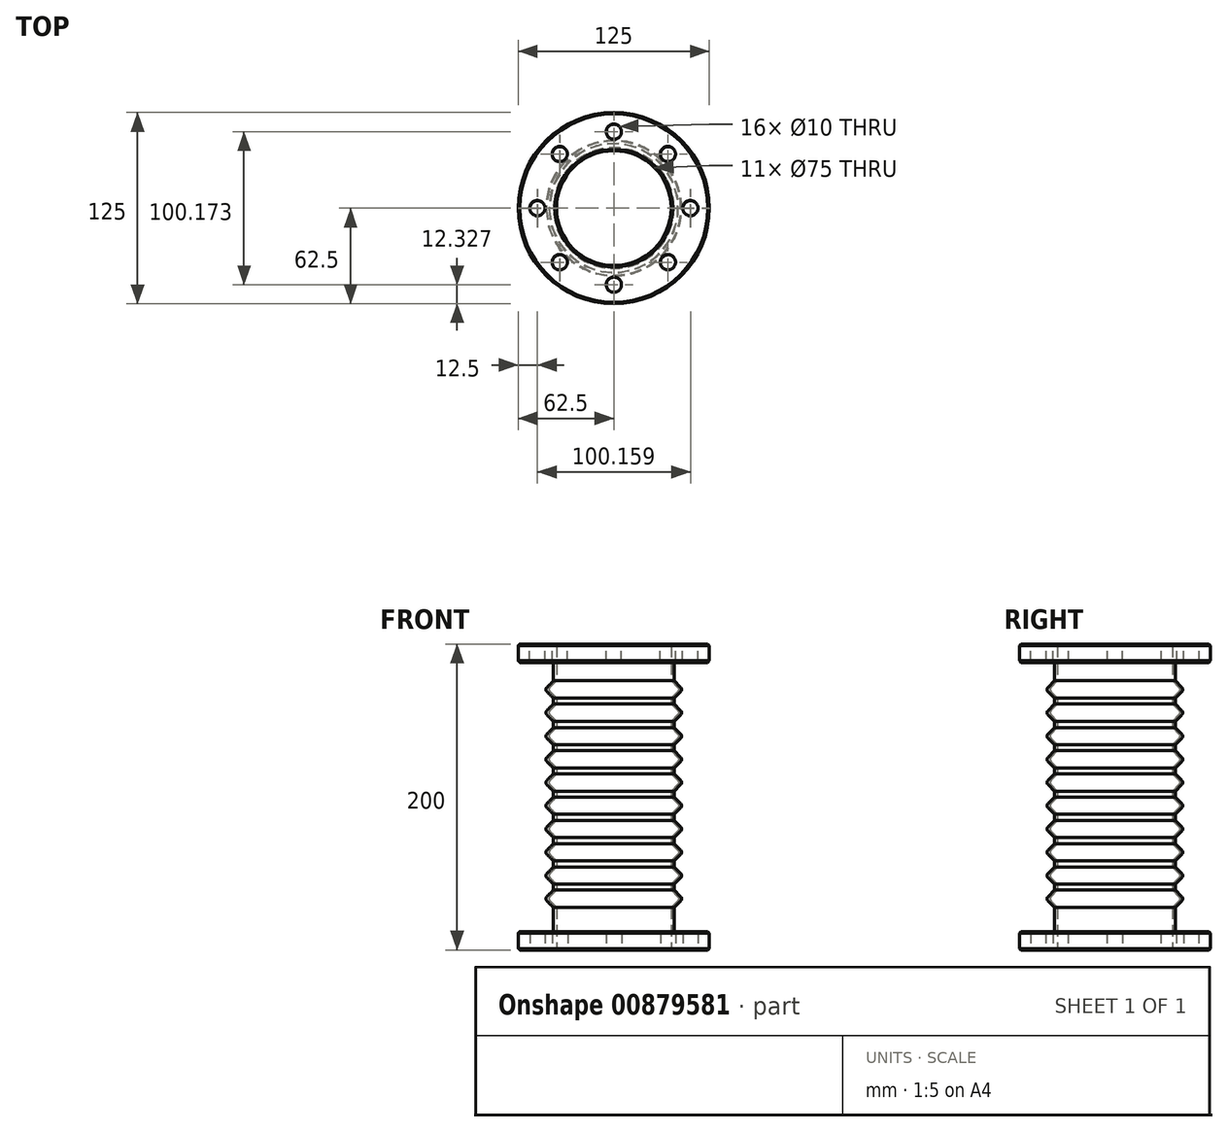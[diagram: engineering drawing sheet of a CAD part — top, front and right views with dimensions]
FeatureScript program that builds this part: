
annotation { "Feature Type Name" : "Feature", "Feature Type Description" : "" }
export const myFeature = defineFeature(function(context is Context, id is Id, definition is map)
    precondition{}
    {
        {
            var Q0;
            Q0=qCreatedBy(makeId("Front.planeOp"),FACE);
            var sketch = newSketch(context, id + "F0", { "sketchPlane" : qUnion([Q0])});
            skLineSegment(sketch, "E0", {"start": v(0, 0) * mm, "end": v(0, 200) * mm, "construction": true});
            skLineSegment(sketch, "E1.bottom", {"start": v(37.5, 0) * mm, "end": v(62.5, 0) * mm});
            skLineSegment(sketch, "E1.top", {"start": v(37.5, 12) * mm, "end": v(62.5, 12) * mm});
            skLineSegment(sketch, "E1.left", {"start": v(37.5, 0) * mm, "end": v(37.5, 12) * mm});
            skLineSegment(sketch, "E1.right", {"start": v(62.5, 0) * mm, "end": v(62.5, 12) * mm});
            skLineSegment(sketch, "E2.bottom", {"start": v(37.5, 188) * mm, "end": v(62.5, 188) * mm});
            skLineSegment(sketch, "E2.top", {"start": v(37.5, 200) * mm, "end": v(62.5, 200) * mm});
            skLineSegment(sketch, "E2.left", {"start": v(37.5, 188) * mm, "end": v(37.5, 200) * mm});
            skLineSegment(sketch, "E2.right", {"start": v(62.5, 188) * mm, "end": v(62.5, 200) * mm});
            skLineSegment(sketch, "E3", {"start": v(49.12, 188) * mm, "end": v(37.5, 188) * mm});
            skLineSegment(sketch, "E4", {"start": v(37.5, 12) * mm, "end": v(37.5, 24) * mm});
            skLineSegment(sketch, "E5", {"start": v(37.5, 176.04) * mm, "end": v(41.74, 171.8) * mm});
            skLineSegment(sketch, "E6", {"start": v(41.74, 168.97) * mm, "end": v(37.5, 164.73) * mm});
            skLineSegment(sketch, "E7", {"start": v(37.5, 160.85) * mm, "end": v(41.74, 156.61) * mm});
            skLineSegment(sketch, "E8", {"start": v(41.74, 153.78) * mm, "end": v(37.5, 149.54) * mm});
            skLineSegment(sketch, "E9", {"start": v(37.5, 145.51) * mm, "end": v(41.74, 141.27) * mm});
            skLineSegment(sketch, "E10", {"start": v(41.74, 138.44) * mm, "end": v(37.5, 134.2) * mm});
            skLineSegment(sketch, "E11", {"start": v(37.5, 130.3) * mm, "end": v(41.74, 126.06) * mm});
            skLineSegment(sketch, "E12", {"start": v(41.74, 123.24) * mm, "end": v(37.5, 119) * mm});
            skLineSegment(sketch, "E13", {"start": v(37.5, 119) * mm, "end": v(37.5, 115.1) * mm});
            skLineSegment(sketch, "E14", {"start": v(37.5, 115.14) * mm, "end": v(41.74, 110.9) * mm});
            skLineSegment(sketch, "E15", {"start": v(41.74, 108.07) * mm, "end": v(37.5, 103.82) * mm});
            skLineSegment(sketch, "E16", {"start": v(37.5, 100.01) * mm, "end": v(41.74, 95.77) * mm});
            skLineSegment(sketch, "E17", {"start": v(41.74, 92.94) * mm, "end": v(37.5, 88.7) * mm});
            skLineSegment(sketch, "E18", {"start": v(37.5, 88.7) * mm, "end": v(37.5, 84.81) * mm});
            skLineSegment(sketch, "E19", {"start": v(41.75, 77.7) * mm, "end": v(37.5, 73.45) * mm});
            skLineSegment(sketch, "E20", {"start": v(37.5, 73.45) * mm, "end": v(37.5, 69.56) * mm});
            skLineSegment(sketch, "E21", {"start": v(41.74, 62.48) * mm, "end": v(37.5, 58.24) * mm});
            skLineSegment(sketch, "E22", {"start": v(37.5, 58.24) * mm, "end": v(37.5, 54.35) * mm});
            skLineSegment(sketch, "E23", {"start": v(41.75, 47.23) * mm, "end": v(37.5, 42.98) * mm});
            skLineSegment(sketch, "E24", {"start": v(37.5, 42.98) * mm, "end": v(37.5, 39.1) * mm});
            skLineSegment(sketch, "E25", {"start": v(37.5, 39.2) * mm, "end": v(41.74, 34.96) * mm});
            skLineSegment(sketch, "E26", {"start": v(41.74, 32.13) * mm, "end": v(37.5, 27.89) * mm});
            skLineSegment(sketch, "E27", {"start": v(37.5, 27.89) * mm, "end": v(37.5, 24) * mm});
            skLineSegment(sketch, "E28", {"start": v(43.74, 168.93) * mm, "end": v(39.5, 164.69) * mm});
            skLineSegment(sketch, "E29", {"start": v(39.5, 164.69) * mm, "end": v(39.5, 160.8) * mm});
            skLineSegment(sketch, "E30", {"start": v(39.5, 160.82) * mm, "end": v(43.74, 156.57) * mm});
            skLineSegment(sketch, "E31", {"start": v(43.74, 153.74) * mm, "end": v(39.44, 149.44) * mm});
            skLineSegment(sketch, "E32", {"start": v(39.44, 149.44) * mm, "end": v(39.44, 145.44) * mm});
            skLineSegment(sketch, "E33", {"start": v(43.73, 138.4) * mm, "end": v(39.5, 134.16) * mm});
            skLineSegment(sketch, "E34", {"start": v(39.5, 134.16) * mm, "end": v(39.5, 130.27) * mm});
            skLineSegment(sketch, "E35", {"start": v(43.74, 123.2) * mm, "end": v(39.5, 118.95) * mm});
            skLineSegment(sketch, "E36", {"start": v(39.5, 118.95) * mm, "end": v(39.5, 115.07) * mm});
            skLineSegment(sketch, "E37", {"start": v(39.5, 115.14) * mm, "end": v(43.74, 110.9) * mm});
            skLineSegment(sketch, "E38", {"start": v(43.74, 108.07) * mm, "end": v(39.5, 103.82) * mm});
            skLineSegment(sketch, "E39", {"start": v(39.5, 103.82) * mm, "end": v(39.5, 99.94) * mm});
            skLineSegment(sketch, "E40", {"start": v(39.5, 100.01) * mm, "end": v(43.74, 95.77) * mm});
            skLineSegment(sketch, "E41", {"start": v(43.74, 92.94) * mm, "end": v(39.5, 88.7) * mm});
            skLineSegment(sketch, "E42", {"start": v(39.5, 88.7) * mm, "end": v(39.5, 84.81) * mm});
            skLineSegment(sketch, "E43", {"start": v(43.75, 77.7) * mm, "end": v(39.5, 73.45) * mm});
            skLineSegment(sketch, "E44", {"start": v(39.5, 73.45) * mm, "end": v(39.5, 69.56) * mm});
            skLineSegment(sketch, "E45", {"start": v(43.74, 62.48) * mm, "end": v(39.5, 58.24) * mm});
            skLineSegment(sketch, "E46", {"start": v(39.5, 58.24) * mm, "end": v(39.5, 54.35) * mm});
            skLineSegment(sketch, "E47", {"start": v(43.75, 47.23) * mm, "end": v(39.5, 42.98) * mm});
            skLineSegment(sketch, "E48", {"start": v(39.5, 42.98) * mm, "end": v(39.5, 39.1) * mm});
            skLineSegment(sketch, "E49", {"start": v(39.5, 39.2) * mm, "end": v(43.74, 34.96) * mm});
            skLineSegment(sketch, "E50", {"start": v(43.74, 32.13) * mm, "end": v(39.5, 27.89) * mm});
            skLineSegment(sketch, "E51", {"start": v(43.74, 171.76) * mm, "end": v(39.5, 176) * mm});
            skLineSegment(sketch, "E52", {"start": v(39.5, 27.89) * mm, "end": v(39.5, 24) * mm});
            skLineSegment(sketch, "E53", {"start": v(37.5, 100.01) * mm, "end": v(37.5, 103.82) * mm});
            skLineSegment(sketch, "E54", {"start": v(37.5, 130.3) * mm, "end": v(37.5, 134.2) * mm});
            skLineSegment(sketch, "E55", {"start": v(37.5, 145.51) * mm, "end": v(37.5, 149.54) * mm});
            skLineSegment(sketch, "E56", {"start": v(37.5, 160.85) * mm, "end": v(37.5, 164.73) * mm});
            skLineSegment(sketch, "E57", {"start": v(39.5, 176) * mm, "end": v(39.5, 188) * mm});
            skLineSegment(sketch, "E58", {"start": v(37.5, 176.04) * mm, "end": v(37.5, 188) * mm});
            skLineSegment(sketch, "E59", {"start": v(39.5, 24) * mm, "end": v(39.5, 12) * mm});
            skLineSegment(sketch, "E60", {"start": v(39.5, 12) * mm, "end": v(39.5, 27.89) * mm});
            skLineSegment(sketch, "E61", {"start": v(39.44, 145.44) * mm, "end": v(43.72, 141.23) * mm});
            skLineSegment(sketch, "E62", {"start": v(43.74, 126.02) * mm, "end": v(39.5, 130.27) * mm});
            skLineSegment(sketch, "E63", {"start": v(43.76, 80.52) * mm, "end": v(39.5, 84.81) * mm});
            skLineSegment(sketch, "E64", {"start": v(41.76, 80.52) * mm, "end": v(37.5, 84.81) * mm});
            skLineSegment(sketch, "E65", {"start": v(39.5, 69.56) * mm, "end": v(43.75, 65.3) * mm});
            skLineSegment(sketch, "E66", {"start": v(37.5, 69.56) * mm, "end": v(41.75, 65.3) * mm});
            skLineSegment(sketch, "E67", {"start": v(41.76, 50.05) * mm, "end": v(37.5, 54.35) * mm});
            skLineSegment(sketch, "E68", {"start": v(43.76, 50.05) * mm, "end": v(39.5, 54.35) * mm});
            skPoint(sketch, "E69.visualSharp", {"position": v(43.16, 170.38) * mm});
            skArc(sketch, "E69.filletArc", {"start": v(41.74, 168.97) * mm, "mid": v(42.33, 170.38) * mm, "end": v(41.74, 171.8) * mm});
            skPoint(sketch, "E70.visualSharp", {"position": v(45.16, 170.34) * mm});
            skArc(sketch, "E70.filletArc", {"start": v(43.74, 168.93) * mm, "mid": v(44.33, 170.34) * mm, "end": v(43.74, 171.76) * mm});
            skPoint(sketch, "E71.visualSharp", {"position": v(43.16, 155.2) * mm});
            skArc(sketch, "E71.filletArc", {"start": v(41.74, 153.78) * mm, "mid": v(42.33, 155.2) * mm, "end": v(41.74, 156.61) * mm});
            skPoint(sketch, "E72.visualSharp", {"position": v(45.16, 155.16) * mm});
            skArc(sketch, "E72.filletArc", {"start": v(43.74, 153.74) * mm, "mid": v(44.33, 155.16) * mm, "end": v(43.74, 156.57) * mm});
            skPoint(sketch, "E73.visualSharp", {"position": v(43.16, 139.86) * mm});
            skArc(sketch, "E73.filletArc", {"start": v(41.74, 138.44) * mm, "mid": v(42.33, 139.86) * mm, "end": v(41.74, 141.27) * mm});
            skPoint(sketch, "E74.visualSharp", {"position": v(45.16, 139.82) * mm});
            skArc(sketch, "E74.filletArc", {"start": v(43.73, 138.4) * mm, "mid": v(44.32, 139.81) * mm, "end": v(43.72, 141.23) * mm});
            skPoint(sketch, "E75.visualSharp", {"position": v(43.16, 124.65) * mm});
            skArc(sketch, "E75.filletArc", {"start": v(41.74, 123.24) * mm, "mid": v(42.33, 124.65) * mm, "end": v(41.74, 126.06) * mm});
            skPoint(sketch, "E76.visualSharp", {"position": v(45.16, 124.61) * mm});
            skArc(sketch, "E76.filletArc", {"start": v(43.74, 123.2) * mm, "mid": v(44.33, 124.61) * mm, "end": v(43.74, 126.02) * mm});
            skPoint(sketch, "E77.visualSharp", {"position": v(43.16, 109.48) * mm});
            skArc(sketch, "E77.filletArc", {"start": v(41.74, 108.07) * mm, "mid": v(42.33, 109.48) * mm, "end": v(41.74, 110.9) * mm});
            skPoint(sketch, "E78.visualSharp", {"position": v(45.16, 109.48) * mm});
            skArc(sketch, "E78.filletArc", {"start": v(43.74, 108.07) * mm, "mid": v(44.33, 109.48) * mm, "end": v(43.74, 110.9) * mm});
            skPoint(sketch, "E79.visualSharp", {"position": v(43.16, 94.35) * mm});
            skArc(sketch, "E79.filletArc", {"start": v(41.74, 92.94) * mm, "mid": v(42.33, 94.35) * mm, "end": v(41.74, 95.77) * mm});
            skPoint(sketch, "E80.visualSharp", {"position": v(45.16, 94.35) * mm});
            skArc(sketch, "E80.filletArc", {"start": v(43.74, 92.94) * mm, "mid": v(44.33, 94.35) * mm, "end": v(43.74, 95.77) * mm});
            skPoint(sketch, "E81.visualSharp", {"position": v(43.16, 79.1) * mm});
            skArc(sketch, "E81.filletArc", {"start": v(41.75, 77.7) * mm, "mid": v(42.33, 79.1) * mm, "end": v(41.76, 80.52) * mm});
            skPoint(sketch, "E82.visualSharp", {"position": v(45.16, 79.1) * mm});
            skArc(sketch, "E82.filletArc", {"start": v(43.75, 77.7) * mm, "mid": v(44.33, 79.1) * mm, "end": v(43.76, 80.52) * mm});
            skPoint(sketch, "E83.visualSharp", {"position": v(43.16, 63.9) * mm});
            skArc(sketch, "E83.filletArc", {"start": v(41.74, 62.48) * mm, "mid": v(42.33, 63.9) * mm, "end": v(41.75, 65.3) * mm});
            skPoint(sketch, "E84.visualSharp", {"position": v(45.16, 63.9) * mm});
            skArc(sketch, "E84.filletArc", {"start": v(43.74, 62.48) * mm, "mid": v(44.33, 63.9) * mm, "end": v(43.75, 65.3) * mm});
            skPoint(sketch, "E85.visualSharp", {"position": v(43.16, 48.64) * mm});
            skArc(sketch, "E85.filletArc", {"start": v(41.75, 47.23) * mm, "mid": v(42.34, 48.64) * mm, "end": v(41.76, 50.05) * mm});
            skPoint(sketch, "E86.visualSharp", {"position": v(45.16, 48.64) * mm});
            skArc(sketch, "E86.filletArc", {"start": v(43.75, 47.23) * mm, "mid": v(44.34, 48.64) * mm, "end": v(43.76, 50.05) * mm});
            skPoint(sketch, "E87.visualSharp", {"position": v(43.16, 33.54) * mm});
            skArc(sketch, "E87.filletArc", {"start": v(41.74, 32.13) * mm, "mid": v(42.33, 33.54) * mm, "end": v(41.74, 34.96) * mm});
            skPoint(sketch, "E88.visualSharp", {"position": v(45.16, 33.54) * mm});
            skArc(sketch, "E88.filletArc", {"start": v(43.74, 32.13) * mm, "mid": v(44.33, 33.54) * mm, "end": v(43.74, 34.96) * mm});
            skSolve(sketch);
        }
        {
            var Q0;
            {var subQ0=sQuery(id+"F0.wireOp",EDGE,"7JNMCSmd-nJx8-slAp-5Nux-Cu1BHQG4eeL3");Q0=makeQuery(id+"F0.imprint","IMPRINT",FACE,{"disambiguationData":[TD([[makeQuery(id+"F0.imprint","IMPRINT",EDGE,{"derivedFrom":subQ0}),-1.0]])]});}
            var Q1;
            Q1=makeQuery(id+"F0.imprint","IMPRINT",FACE,{"disambiguationData":[TD([[makeQuery(id+"F0.imprint","IMPRINT",EDGE,{"derivedFrom":sQuery(id+"F0.wireOp",EDGE,"E2.bottom")}),1.0]])]});
            var Q2;
            Q2=makeQuery(id+"F0.imprint","IMPRINT",FACE,{"disambiguationData":[TD([[makeQuery(id+"F0.imprint","IMPRINT",EDGE,{"derivedFrom":sQuery(id+"F0.wireOp",EDGE,"E1.bottom")}),1.0]])]});
            var Q3;
            {var subQ13=sQuery(id+"F0.wireOp",EDGE,"E4");Q3=makeQuery(id+"F0.imprint","IMPRINT",FACE,{"disambiguationData":[TD([[makeQuery(id+"F0.imprint","IMPRINT",EDGE,{"derivedFrom":subQ13}),-1.0]])]});}
            var Q4;
            Q4=sQuery(id+"F0.wireOp",EDGE,"E0");
            revolve(context, id + "F1", {"surfaceOperationType" : NewSurfaceOperationType.NEW, "entities" : qUnion([Q0, Q1, Q2, Q3]), "axis" : qUnion([Q4]), "revolveType" : RevolveType.FULL});
        }
        {
            var Q0;
            Q0=makeQuery(id+"F1.opRevolve","SWEPT_FACE",FACE,{"disambiguationData":[OSD([sQuery(id+"F0.wireOp",EDGE,"E2.top")])]});
            var sketch = newSketch(context, id + "F2", { "sketchPlane" : qUnion([Q0])});
            skCircle(sketch, "E89", {"center": v(0, 0) * mm, "radius": 50 * mm});
            skLineSegment(sketch, "E90", {"start": v(0, 0) * mm, "end": v(-50, 0) * mm});
            skLineSegment(sketch, "E91", {"start": v(0, 0) * mm, "end": v(0, 50) * mm});
            skLineSegment(sketch, "E92", {"start": v(0, 0) * mm, "end": v(-35.36, 35.36) * mm});
            skLineSegment(sketch, "E93", {"start": v(0, 0) * mm, "end": v(50, 0) * mm});
            skLineSegment(sketch, "E94", {"start": v(0, 0) * mm, "end": v(35.36, 35.36) * mm});
            skLineSegment(sketch, "E95", {"start": v(0, 0) * mm, "end": v(35.36, -35.36) * mm});
            skLineSegment(sketch, "E96", {"start": v(0, 0) * mm, "end": v(0, -50) * mm});
            skLineSegment(sketch, "E97", {"start": v(0, 0) * mm, "end": v(-35.36, -35.36) * mm});
            skSolve(sketch);
        }
        {
            var Q0;
            Q0=sQuery(id+"F2.wireOp",VERTEX,"E90.end");
            var Q1;
            Q1=sQuery(id+"F2.wireOp",VERTEX,"E92.end");
            var Q2;
            Q2=sQuery(id+"F2.wireOp",VERTEX,"E91.end");
            var Q3;
            Q3=sQuery(id+"F2.wireOp",VERTEX,"E94.end");
            var Q4;
            Q4=sQuery(id+"F2.wireOp",VERTEX,"E93.end");
            var Q5;
            Q5=sQuery(id+"F2.wireOp",VERTEX,"E95.end");
            var Q6;
            Q6=sQuery(id+"F2.wireOp",VERTEX,"E96.end");
            var Q7;
            Q7=sQuery(id+"F2.wireOp",VERTEX,"E97.end");
            var Q8;
            Q8=makeQuery(id+"F1.opRevolve","SWEPT_BODY",BODY,{"disambiguationData":[OSD([sQuery(id+"F0.wireOp",EDGE,"E1.bottom"),sQuery(id+"F0.wireOp",EDGE,"E1.top"),sQuery(id+"F0.wireOp",EDGE,"E1.left"),sQuery(id+"F0.wireOp",EDGE,"E1.right"),sQuery(id+"F0.wireOp",EDGE,"E2.bottom"),sQuery(id+"F0.wireOp",EDGE,"E2.top"),sQuery(id+"F0.wireOp",EDGE,"E2.left"),sQuery(id+"F0.wireOp",EDGE,"E2.right"),sQuery(id+"F0.wireOp",EDGE,"7JNMCSmd-nJx8-slAp-5Nux-Cu1BHQG4eeL3"),sQuery(id+"F0.wireOp",EDGE,"xSUHY1hX-u8nV-SjKD-2nK2-6XUFaaVvMroe"),sQuery(id+"F0.wireOp",EDGE,"rQDTT3AA-Bt1S-jRNE-MUDb-fmsf6ePG7gEG"),sQuery(id+"F0.wireOp",EDGE,"25a1cL4V-paF4-rwCJ-306o-4v5FNgoqHX95"),sQuery(id+"F0.wireOp",EDGE,"bOkS3g0W-cvPP-gkzR-AXlQ-F5RIaoCkBvoo"),sQuery(id+"F0.wireOp",EDGE,"DAgTOG4h-LVyY-aJrt-t6WS-GQ4c7HnX23bk"),sQuery(id+"F0.wireOp",EDGE,"wgsqm14R-cCDp-ybnt-tiYT-U1sHfBOHY4Df"),sQuery(id+"F0.wireOp",EDGE,"77dda6b8-0e61-492f-92f8-d2d185dd74d5.filletArc"),sQuery(id+"F0.wireOp",EDGE,"0257c514-efe3-423c-bb2b-4c4e0ae5e3d5.filletArc"),sQuery(id+"F0.wireOp",EDGE,"e251e59c-608a-4d9b-9d9d-7884a468bad4.filletArc"),sQuery(id+"F0.wireOp",EDGE,"1fcf53c9-d44e-426e-92d8-455222d8480c.filletArc"),sQuery(id+"F0.wireOp",EDGE,"723f02ad-6a34-478a-827c-48895c4f980a.filletArc"),sQuery(id+"F0.wireOp",EDGE,"36326b0e-995e-4fdb-9748-851bf4a9242e.filletArc"),sQuery(id+"F0.wireOp",EDGE,"f7893906-4d7b-4bea-b248-10763c51d39d.0"),sQuery(id+"F0.wireOp",EDGE,"f7893906-4d7b-4bea-b248-10763c51d39d.1"),sQuery(id+"F0.wireOp",EDGE,"f7893906-4d7b-4bea-b248-10763c51d39d.2"),sQuery(id+"F0.wireOp",EDGE,"f7893906-4d7b-4bea-b248-10763c51d39d.3"),sQuery(id+"F0.wireOp",EDGE,"f7893906-4d7b-4bea-b248-10763c51d39d.4"),sQuery(id+"F0.wireOp",EDGE,"f7893906-4d7b-4bea-b248-10763c51d39d.5"),sQuery(id+"F0.wireOp",EDGE,"f7893906-4d7b-4bea-b248-10763c51d39d.6"),sQuery(id+"F0.wireOp",EDGE,"f7893906-4d7b-4bea-b248-10763c51d39d.7"),sQuery(id+"F0.wireOp",EDGE,"f7893906-4d7b-4bea-b248-10763c51d39d.8"),sQuery(id+"F0.wireOp",EDGE,"f7893906-4d7b-4bea-b248-10763c51d39d.9"),sQuery(id+"F0.wireOp",EDGE,"f7893906-4d7b-4bea-b248-10763c51d39d.10"),sQuery(id+"F0.wireOp",EDGE,"zz77thpP-ZF6f-9Xch-fK0u-6JuafN0EIoVi"),sQuery(id+"F0.wireOp",EDGE,"MnvxiiVR-vjBi-grum-E19G-Wj8JN0Ya69Xf")])]});
            hole(context, id + "F3", {"style" : HoleStyle.SIMPLE, "endStyle" : HoleEndStyle.BLIND, "holeDiameter" : 10 * mm, "majorDiameter" : 5 * mm, "holeDepth" : 20 * mm, "isTappedThrough" : true, "tappedDepth" : 12 * mm, "tapClearance" : 3, "locations" : qUnion([Q0, Q1, Q2, Q3, Q4, Q5, Q6, Q7]), "scope" : qUnion([Q8])});
        }
        {
            var Q0;
            Q0=makeQuery(id+"F1.opRevolve","SWEPT_FACE",FACE,{"disambiguationData":[OSD([sQuery(id+"F0.wireOp",EDGE,"E1.bottom")])]});
            var sketch = newSketch(context, id + "F4", { "sketchPlane" : qUnion([Q0])});
            skCircle(sketch, "E98", {"center": v(0.16, 0.17) * mm, "radius": 50 * mm});
            skLineSegment(sketch, "E99", {"start": v(0.16, 0.17) * mm, "end": v(-49.84, 0.17) * mm});
            skLineSegment(sketch, "E100", {"start": v(0.16, 0.17) * mm, "end": v(0.16, 50.17) * mm});
            skLineSegment(sketch, "E101", {"start": v(0.16, 0.17) * mm, "end": v(-35.2, 35.53) * mm});
            skLineSegment(sketch, "E102", {"start": v(0.16, 0.17) * mm, "end": v(50.16, 0.17) * mm});
            skLineSegment(sketch, "E103", {"start": v(0.16, 0.17) * mm, "end": v(35.51, 35.53) * mm});
            skLineSegment(sketch, "E104", {"start": v(0.16, 0.17) * mm, "end": v(35.51, -35.18) * mm});
            skLineSegment(sketch, "E105", {"start": v(0.16, 0.17) * mm, "end": v(0.16, -49.83) * mm});
            skLineSegment(sketch, "E106", {"start": v(0.16, 0.17) * mm, "end": v(-35.2, -35.18) * mm});
            skSolve(sketch);
        }
        {
            var Q0;
            Q0=sQuery(id+"F4.wireOp",VERTEX,"E105.end");
            var Q1;
            Q1=sQuery(id+"F4.wireOp",VERTEX,"E106.end");
            var Q2;
            Q2=sQuery(id+"F4.wireOp",VERTEX,"E99.end");
            var Q3;
            Q3=sQuery(id+"F4.wireOp",VERTEX,"E101.end");
            var Q4;
            Q4=sQuery(id+"F4.wireOp",VERTEX,"E100.end");
            var Q5;
            Q5=sQuery(id+"F4.wireOp",VERTEX,"E103.end");
            var Q6;
            Q6=sQuery(id+"F4.wireOp",VERTEX,"E102.end");
            var Q7;
            Q7=sQuery(id+"F4.wireOp",VERTEX,"E104.end");
            var Q8;
            Q8=makeQuery(id+"F1.opRevolve","SWEPT_BODY",BODY,{"disambiguationData":[OSD([sQuery(id+"F0.wireOp",EDGE,"E1.bottom"),sQuery(id+"F0.wireOp",EDGE,"E1.top"),sQuery(id+"F0.wireOp",EDGE,"E1.left"),sQuery(id+"F0.wireOp",EDGE,"E1.right"),sQuery(id+"F0.wireOp",EDGE,"E2.bottom"),sQuery(id+"F0.wireOp",EDGE,"E2.top"),sQuery(id+"F0.wireOp",EDGE,"E2.left"),sQuery(id+"F0.wireOp",EDGE,"E2.right"),sQuery(id+"F0.wireOp",EDGE,"7JNMCSmd-nJx8-slAp-5Nux-Cu1BHQG4eeL3"),sQuery(id+"F0.wireOp",EDGE,"xSUHY1hX-u8nV-SjKD-2nK2-6XUFaaVvMroe"),sQuery(id+"F0.wireOp",EDGE,"rQDTT3AA-Bt1S-jRNE-MUDb-fmsf6ePG7gEG"),sQuery(id+"F0.wireOp",EDGE,"25a1cL4V-paF4-rwCJ-306o-4v5FNgoqHX95"),sQuery(id+"F0.wireOp",EDGE,"bOkS3g0W-cvPP-gkzR-AXlQ-F5RIaoCkBvoo"),sQuery(id+"F0.wireOp",EDGE,"DAgTOG4h-LVyY-aJrt-t6WS-GQ4c7HnX23bk"),sQuery(id+"F0.wireOp",EDGE,"wgsqm14R-cCDp-ybnt-tiYT-U1sHfBOHY4Df"),sQuery(id+"F0.wireOp",EDGE,"77dda6b8-0e61-492f-92f8-d2d185dd74d5.filletArc"),sQuery(id+"F0.wireOp",EDGE,"0257c514-efe3-423c-bb2b-4c4e0ae5e3d5.filletArc"),sQuery(id+"F0.wireOp",EDGE,"e251e59c-608a-4d9b-9d9d-7884a468bad4.filletArc"),sQuery(id+"F0.wireOp",EDGE,"1fcf53c9-d44e-426e-92d8-455222d8480c.filletArc"),sQuery(id+"F0.wireOp",EDGE,"723f02ad-6a34-478a-827c-48895c4f980a.filletArc"),sQuery(id+"F0.wireOp",EDGE,"36326b0e-995e-4fdb-9748-851bf4a9242e.filletArc"),sQuery(id+"F0.wireOp",EDGE,"f7893906-4d7b-4bea-b248-10763c51d39d.0"),sQuery(id+"F0.wireOp",EDGE,"f7893906-4d7b-4bea-b248-10763c51d39d.1"),sQuery(id+"F0.wireOp",EDGE,"f7893906-4d7b-4bea-b248-10763c51d39d.2"),sQuery(id+"F0.wireOp",EDGE,"f7893906-4d7b-4bea-b248-10763c51d39d.3"),sQuery(id+"F0.wireOp",EDGE,"f7893906-4d7b-4bea-b248-10763c51d39d.4"),sQuery(id+"F0.wireOp",EDGE,"f7893906-4d7b-4bea-b248-10763c51d39d.5"),sQuery(id+"F0.wireOp",EDGE,"f7893906-4d7b-4bea-b248-10763c51d39d.6"),sQuery(id+"F0.wireOp",EDGE,"f7893906-4d7b-4bea-b248-10763c51d39d.7"),sQuery(id+"F0.wireOp",EDGE,"f7893906-4d7b-4bea-b248-10763c51d39d.8"),sQuery(id+"F0.wireOp",EDGE,"f7893906-4d7b-4bea-b248-10763c51d39d.9"),sQuery(id+"F0.wireOp",EDGE,"f7893906-4d7b-4bea-b248-10763c51d39d.10"),sQuery(id+"F0.wireOp",EDGE,"zz77thpP-ZF6f-9Xch-fK0u-6JuafN0EIoVi"),sQuery(id+"F0.wireOp",EDGE,"MnvxiiVR-vjBi-grum-E19G-Wj8JN0Ya69Xf")])]});
            hole(context, id + "F5", {"style" : HoleStyle.SIMPLE, "endStyle" : HoleEndStyle.BLIND, "holeDiameter" : 10 * mm, "majorDiameter" : 5 * mm, "holeDepth" : 12 * mm, "isTappedThrough" : true, "tappedDepth" : 12 * mm, "tapClearance" : 3, "locations" : qUnion([Q0, Q1, Q2, Q3, Q4, Q5, Q6, Q7]), "scope" : qUnion([Q8])});
        }
        {
            var Q0;
            Q0=makeQuery(id+"F1.opRevolve","SWEPT_EDGE",EDGE,{"disambiguationData":[OSD([sQuery(id+"F0.wireOp",EDGE,"E2.top"),sQuery(id+"F0.wireOp",EDGE,"E2.right")])]});
            var Q1;
            Q1=makeQuery(id+"F1.opRevolve","SWEPT_EDGE",EDGE,{"disambiguationData":[OSD([sQuery(id+"F0.wireOp",EDGE,"E2.top"),sQuery(id+"F0.wireOp",EDGE,"E2.left")])]});
            var Q2;
            Q2=makeQuery(id+"F1.opRevolve","SWEPT_EDGE",EDGE,{"disambiguationData":[OSD([sQuery(id+"F0.wireOp",EDGE,"E2.bottom"),sQuery(id+"F0.wireOp",EDGE,"E2.right")])]});
            var Q3;
            Q3=makeQuery(id+"F1.opRevolve","SWEPT_EDGE",EDGE,{"disambiguationData":[OSD([sQuery(id+"F0.wireOp",EDGE,"E1.top"),sQuery(id+"F0.wireOp",EDGE,"E1.right")])]});
            var Q4;
            Q4=makeQuery(id+"F1.opRevolve","SWEPT_EDGE",EDGE,{"disambiguationData":[OSD([sQuery(id+"F0.wireOp",EDGE,"E1.bottom"),sQuery(id+"F0.wireOp",EDGE,"E1.right")])]});
            chamfer(context, id + "F6", {"entities" : qUnion([Q0, Q1, Q2, Q3, Q4]), "width" : 1 * mm, "tangentPropagation" : true});
        }
    });
